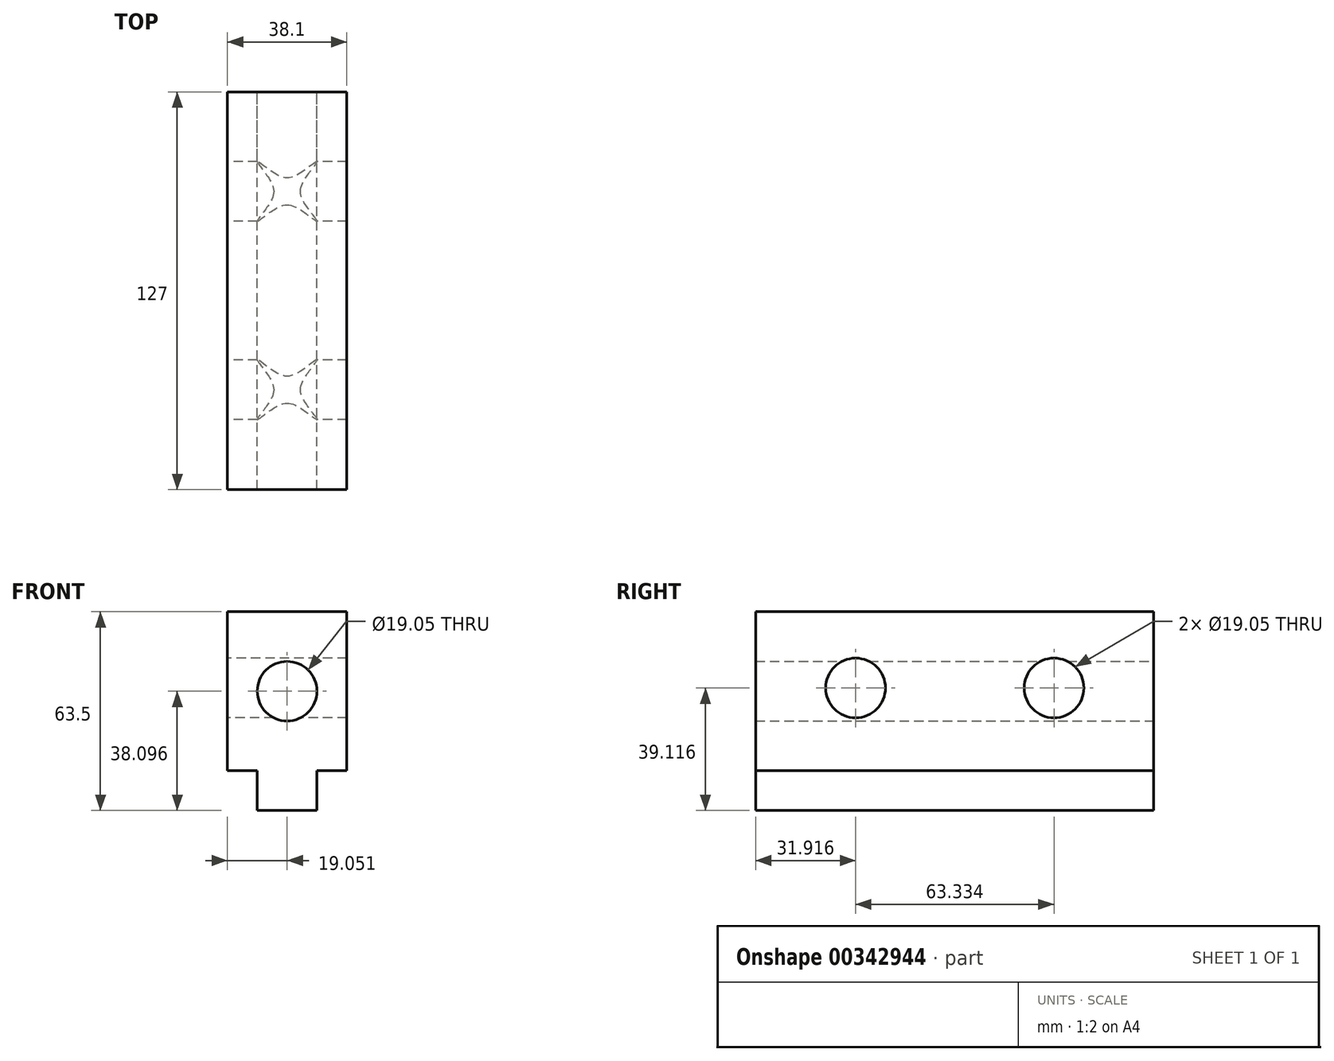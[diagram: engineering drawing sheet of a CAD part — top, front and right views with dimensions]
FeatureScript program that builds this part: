
annotation { "Feature Type Name" : "Feature", "Feature Type Description" : "" }
export const myFeature = defineFeature(function(context is Context, id is Id, definition is map)
    precondition{}
    {
        {
            var Q0;
            Q0=qCreatedBy(makeId("Front.planeOp"),FACE);
            var sketch = newSketch(context, id + "F0", { "sketchPlane" : qUnion([Q0])});
            skLineSegment(sketch, "E0", {"start": v(-31.48, 42.3) * mm, "end": v(-31.48, -8.5) * mm});
            skLineSegment(sketch, "E1", {"start": v(-31.48, 42.3) * mm, "end": v(6.62, 42.3) * mm});
            skLineSegment(sketch, "E2", {"start": v(6.62, 42.3) * mm, "end": v(6.62, -8.5) * mm});
            skLineSegment(sketch, "E3", {"start": v(6.62, -8.5) * mm, "end": v(-2.9, -8.5) * mm});
            skLineSegment(sketch, "E4", {"start": v(-31.48, -8.5) * mm, "end": v(-21.95, -8.5) * mm});
            skLineSegment(sketch, "E5", {"start": v(-21.95, -8.5) * mm, "end": v(-21.95, -21.2) * mm});
            skLineSegment(sketch, "E6", {"start": v(-2.9, -8.5) * mm, "end": v(-2.9, -21.2) * mm});
            skLineSegment(sketch, "E7", {"start": v(-21.95, -21.2) * mm, "end": v(-2.9, -21.2) * mm});
            skCircle(sketch, "E8", {"center": v(-12.43, 16.9) * mm, "radius": 9.53 * mm});
            skSolve(sketch);
        }
        {
            var Q0;
            Q0 = qSketchRegion(id + "F0", true);
            extrude(context, id + "F1", {"entities" : qUnion([Q0]), "depth" : 127 * mm});
        }
        {
            var Q0;
            Q0=qCreatedBy(makeId("Right.planeOp"),FACE);
            var sketch = newSketch(context, id + "F2", { "sketchPlane" : qUnion([Q0])});
            skPoint(sketch, "E9", {"position": v(-126.83, 54.65) * mm});
            skPoint(sketch, "E10", {"position": v(-95.08, 54.65) * mm});
            skCircle(sketch, "E11", {"center": v(-31.75, 17.93) * mm, "radius": 9.53 * mm});
            skCircle(sketch, "E12", {"center": v(-95.08, 17.93) * mm, "radius": 9.53 * mm});
            skPoint(sketch, "E13.start.orphan", {"position": v(0, 77.17) * mm});
            skPoint(sketch, "E14.start.orphan", {"position": v(0, 43.33) * mm});
            skSolve(sketch);
        }
        {
            var Q0;
            Q0 = qSketchRegion(id + "F2", true);
            extrude(context, id + "F3", {"entities" : qUnion([Q0]), "operationType" : NewBodyOperationType.REMOVE, "depth" : 24.9 * mm, "hasSecondDirection" : true, "secondDirectionOppositeDirection" : true, "secondDirectionDepth" : 63 * mm});
        }
    });
